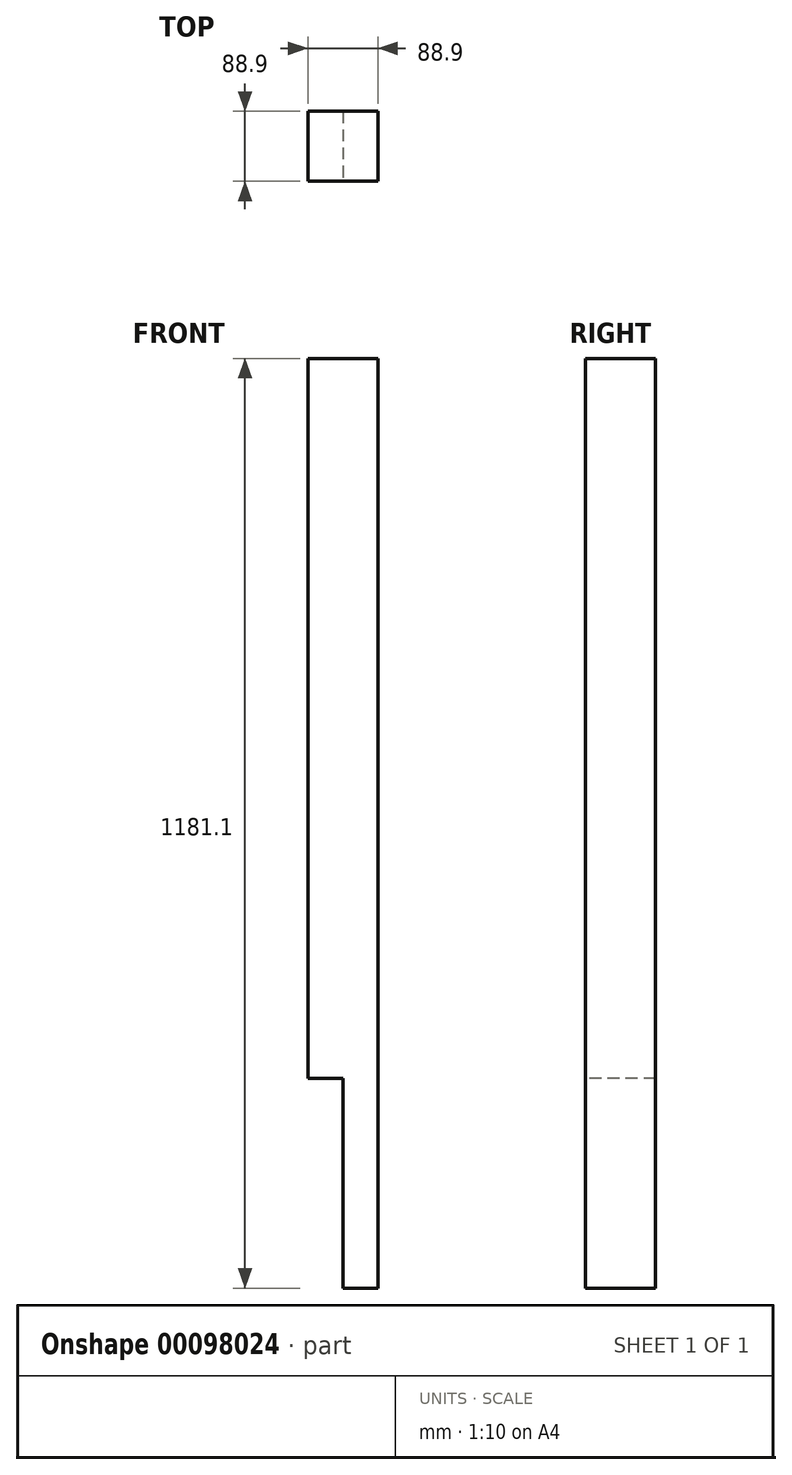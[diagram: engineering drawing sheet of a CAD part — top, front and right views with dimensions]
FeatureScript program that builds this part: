
annotation { "Feature Type Name" : "Feature", "Feature Type Description" : "" }
export const myFeature = defineFeature(function(context is Context, id is Id, definition is map)
    precondition{}
    {
        {
            var Q0;
            Q0=qCreatedBy(makeId("Front.planeOp"),FACE);
            var sketch = newSketch(context, id + "F0", { "sketchPlane" : qUnion([Q0])});
            skLineSegment(sketch, "E0.bottom", {"start": v(44.45, 590.55) * mm, "end": v(-44.45, 590.55) * mm});
            skLineSegment(sketch, "E0.top", {"start": v(44.45, -590.55) * mm, "end": v(-44.45, -590.55) * mm});
            skLineSegment(sketch, "E0.left", {"start": v(44.45, 590.55) * mm, "end": v(44.45, -590.55) * mm});
            skLineSegment(sketch, "E0.right", {"start": v(-44.45, 590.55) * mm, "end": v(-44.45, -590.55) * mm});
            skPoint(sketch, "E0.middle", {"position": v(0, 0) * mm});
            skSolve(sketch);
        }
        {
            var Q0;
            Q0=makeQuery(id+"F0.imprint","IMPRINT",FACE,{"disambiguationData":[TD([[makeQuery(id+"F0.imprint","IMPRINT",EDGE,{"derivedFrom":sQuery(id+"F0.wireOp",EDGE,"E0.bottom")}),1.0]])]});
            extrude(context, id + "F1", {"entities" : qUnion([Q0]), "depth" : 88.9 * mm});
        }
        {
            var Q0;
            Q0=makeQuery(id+"F1.opExtrude","CAP_FACE",FACE,{"disambiguationData":[OSD([sQuery(id+"F0.wireOp",EDGE,"E0.bottom"),sQuery(id+"F0.wireOp",EDGE,"E0.top"),sQuery(id+"F0.wireOp",EDGE,"E0.left"),sQuery(id+"F0.wireOp",EDGE,"E0.right")])],"isStart":false});
            var sketch = newSketch(context, id + "F2", { "sketchPlane" : qUnion([Q0])});
            skLineSegment(sketch, "E1", {"start": v(-44.45, -590.55) * mm, "end": v(-44.45, -323.85) * mm});
            skLineSegment(sketch, "E2", {"start": v(-44.45, -323.85) * mm, "end": v(0, -323.85) * mm});
            skLineSegment(sketch, "E3", {"start": v(0, -323.85) * mm, "end": v(0, -590.55) * mm});
            skLineSegment(sketch, "E4", {"start": v(0, -590.55) * mm, "end": v(-44.45, -590.55) * mm});
            skSolve(sketch);
        }
        {
            var Q0;
            Q0 = qSketchRegion(id + "F2", true);
            extrude(context, id + "F3", {"entities" : qUnion([Q0]), "operationType" : NewBodyOperationType.REMOVE, "endBound" : BoundingType.THROUGH_ALL, "oppositeDirection" : true, "depth" : 25.4 * mm});
        }
    });
